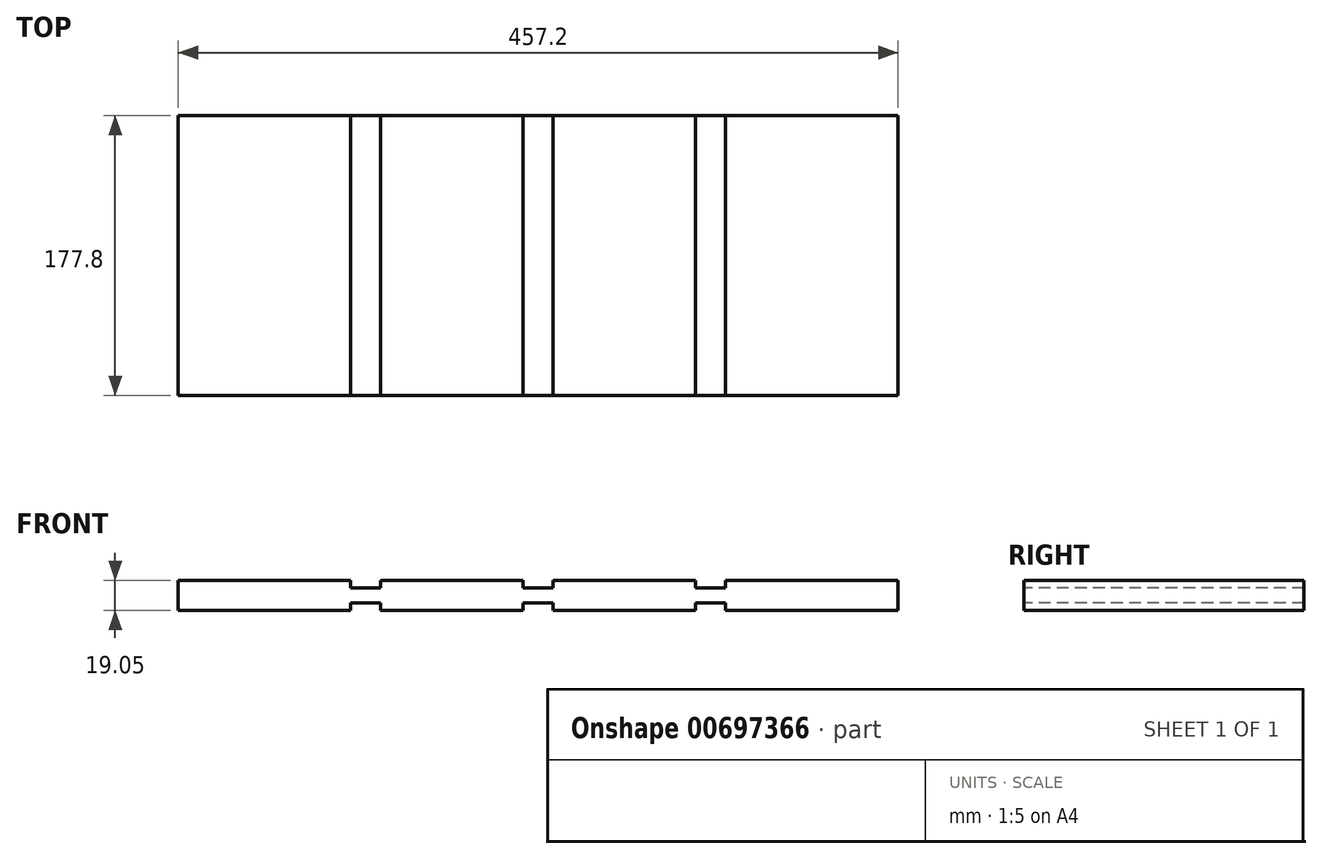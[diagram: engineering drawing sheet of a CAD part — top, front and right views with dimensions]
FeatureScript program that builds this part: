
annotation { "Feature Type Name" : "Feature", "Feature Type Description" : "" }
export const myFeature = defineFeature(function(context is Context, id is Id, definition is map)
    precondition{}
    {
        {
            var Q0;
            Q0=qCreatedBy(makeId("Front.planeOp"),FACE);
            var sketch = newSketch(context, id + "F0", { "sketchPlane" : qUnion([Q0])});
            skLineSegment(sketch, "E0.bottom", {"start": v(0, 0) * mm, "end": v(457.2, 0) * mm});
            skLineSegment(sketch, "E0.top", {"start": v(0, 19.05) * mm, "end": v(457.2, 19.05) * mm});
            skLineSegment(sketch, "E0.left", {"start": v(0, 0) * mm, "end": v(0, 19.05) * mm});
            skLineSegment(sketch, "E0.right", {"start": v(457.2, 0) * mm, "end": v(457.2, 19.05) * mm});
            skSolve(sketch);
        }
        {
            var Q0;
            Q0=qCreatedBy(makeId("Front.planeOp"),FACE);
            var sketch = newSketch(context, id + "F1", { "sketchPlane" : qUnion([Q0])});
            skLineSegment(sketch, "E1.bottom", {"start": v(109.54, 0) * mm, "end": v(128.59, 0) * mm});
            skLineSegment(sketch, "E1.top", {"start": v(109.54, 4.76) * mm, "end": v(128.59, 4.76) * mm});
            skLineSegment(sketch, "E1.left", {"start": v(109.54, 0) * mm, "end": v(109.54, 4.76) * mm});
            skLineSegment(sketch, "E1.right", {"start": v(128.59, 0) * mm, "end": v(128.59, 4.76) * mm});
            skLineSegment(sketch, "E2.1.0.0", {"start": v(219.08, 0) * mm, "end": v(238.13, 0) * mm});
            skLineSegment(sketch, "E2.1.0.1", {"start": v(219.08, 4.76) * mm, "end": v(238.13, 4.76) * mm});
            skLineSegment(sketch, "E2.1.0.2", {"start": v(219.08, 0) * mm, "end": v(219.08, 4.76) * mm});
            skLineSegment(sketch, "E2.1.0.3", {"start": v(238.13, 0) * mm, "end": v(238.13, 4.76) * mm});
            skLineSegment(sketch, "E2.2.0.0", {"start": v(328.61, 0) * mm, "end": v(347.66, 0) * mm});
            skLineSegment(sketch, "E2.2.0.1", {"start": v(328.61, 4.76) * mm, "end": v(347.66, 4.76) * mm});
            skLineSegment(sketch, "E2.2.0.2", {"start": v(328.61, 0) * mm, "end": v(328.61, 4.76) * mm});
            skLineSegment(sketch, "E2.2.0.3", {"start": v(347.66, 0) * mm, "end": v(347.66, 4.76) * mm});
            skLineSegment(sketch, "E2.direction1", {"start": v(109.54, 0) * mm, "end": v(219.08, 0) * mm, "construction": true});
            skSolve(sketch);
        }
        {
            var Q0;
            Q0=qSketchRegion(id+"F0",true);
            extrude(context, id + "F2", {"entities" : qUnion([Q0]), "oppositeDirection" : true, "depth" : 177.8 * mm, "offsetDistance" : 25.4 * mm});
        }
        {
            var Q0;
            Q0=qSketchRegion(id+"F1",true);
            extrude(context, id + "F3", {"entities" : qUnion([Q0]), "operationType" : NewBodyOperationType.REMOVE, "endBound" : BoundingType.THROUGH_ALL, "oppositeDirection" : true, "depth" : 25.4 * mm, "offsetDistance" : 25.4 * mm});
        }
        {
            var Q0;
            Q0=qCreatedBy(makeId("Front.planeOp"),FACE);
            var sketch = newSketch(context, id + "F4", { "sketchPlane" : qUnion([Q0])});
            skLineSegment(sketch, "E3.bottom", {"start": v(109.54, 19.05) * mm, "end": v(128.59, 19.05) * mm});
            skLineSegment(sketch, "E3.top", {"start": v(109.54, 14.29) * mm, "end": v(128.59, 14.29) * mm});
            skLineSegment(sketch, "E3.left", {"start": v(109.54, 19.05) * mm, "end": v(109.54, 14.29) * mm});
            skLineSegment(sketch, "E3.right", {"start": v(128.59, 19.05) * mm, "end": v(128.59, 14.29) * mm});
            skLineSegment(sketch, "E4.1.0.0", {"start": v(219.08, 19.05) * mm, "end": v(219.08, 14.29) * mm});
            skLineSegment(sketch, "E4.1.0.1", {"start": v(238.13, 19.05) * mm, "end": v(238.13, 14.29) * mm});
            skLineSegment(sketch, "E4.1.0.2", {"start": v(219.08, 14.29) * mm, "end": v(238.13, 14.29) * mm});
            skLineSegment(sketch, "E4.1.0.3", {"start": v(219.08, 19.05) * mm, "end": v(238.13, 19.05) * mm});
            skLineSegment(sketch, "E4.2.0.0", {"start": v(328.61, 19.05) * mm, "end": v(328.61, 14.29) * mm});
            skLineSegment(sketch, "E4.2.0.1", {"start": v(347.66, 19.05) * mm, "end": v(347.66, 14.29) * mm});
            skLineSegment(sketch, "E4.2.0.2", {"start": v(328.61, 14.29) * mm, "end": v(347.66, 14.29) * mm});
            skLineSegment(sketch, "E4.2.0.3", {"start": v(328.61, 19.05) * mm, "end": v(347.66, 19.05) * mm});
            skLineSegment(sketch, "E4.direction1", {"start": v(109.54, 14.29) * mm, "end": v(219.08, 14.29) * mm, "construction": true});
            skSolve(sketch);
        }
        {
            var Q0;
            Q0 = qSketchRegion(id + "F4", true);
            extrude(context, id + "F5", {"entities" : qUnion([Q0]), "operationType" : NewBodyOperationType.REMOVE, "endBound" : BoundingType.THROUGH_ALL, "oppositeDirection" : true, "depth" : 25.4 * mm, "offsetDistance" : 25.4 * mm});
        }
    });
